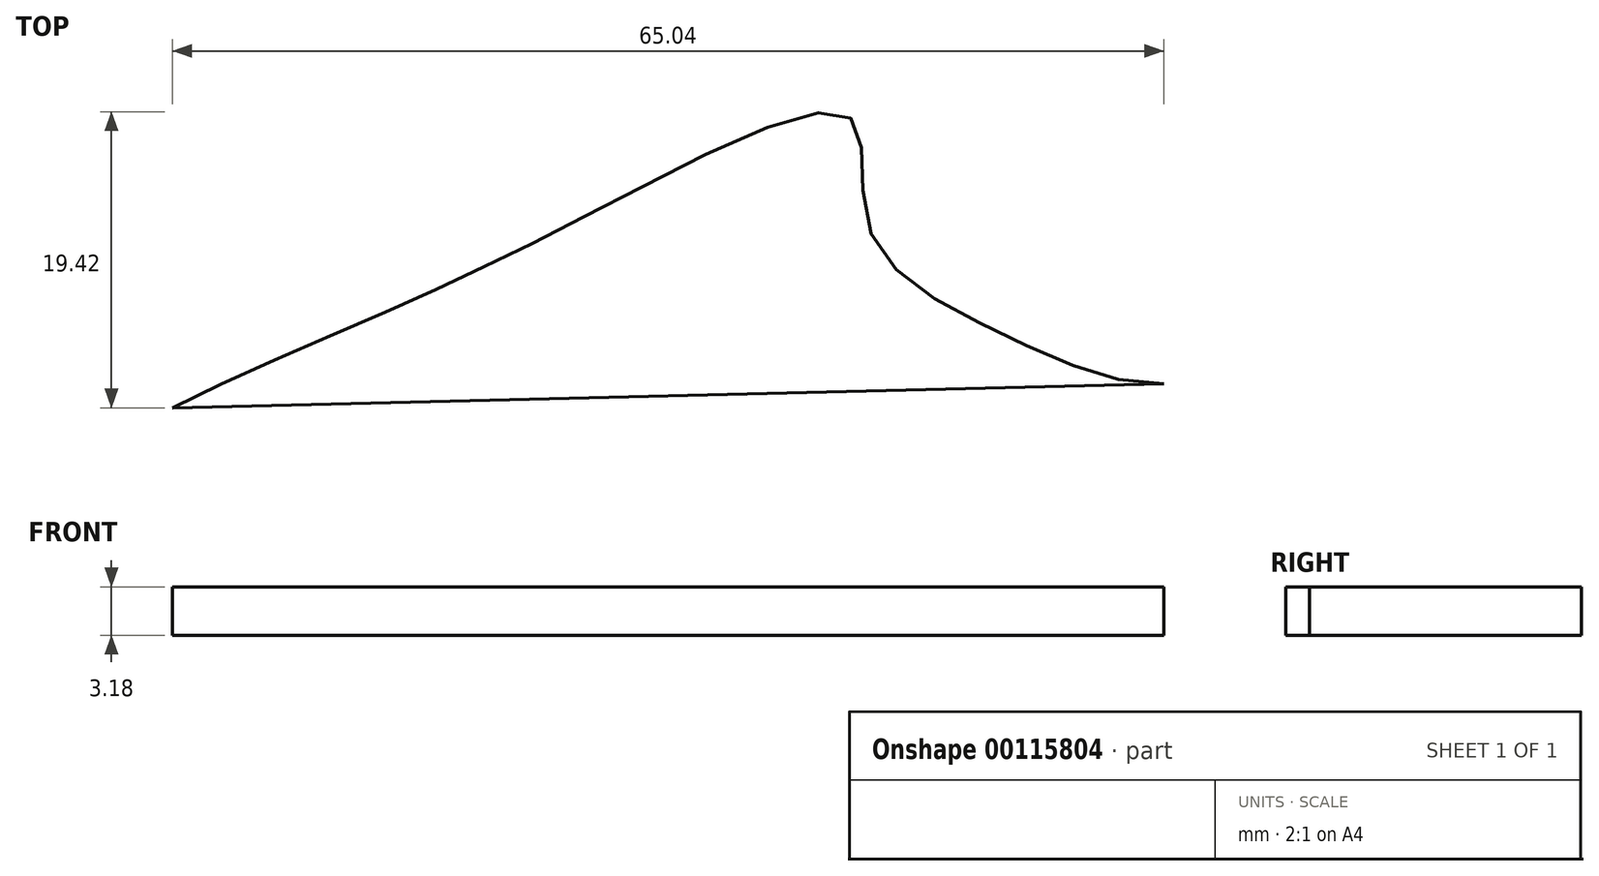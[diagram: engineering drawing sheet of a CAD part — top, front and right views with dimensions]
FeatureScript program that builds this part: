
annotation { "Feature Type Name" : "Feature", "Feature Type Description" : "" }
export const myFeature = defineFeature(function(context is Context, id is Id, definition is map)
    precondition{}
    {
        {
            var Q0;
            Q0=qCreatedBy(makeId("Top.planeOp"),FACE);
            var sketch = newSketch(context, id + "F0", { "sketchPlane" : qUnion([Q0])});
            skFitSpline(sketch, "E0", {"points": [v(-38.84, 12.13) * mm, v(-23.52, 19.01) * mm, v(-9.45, 25.9) * mm, v(5.56, 31.2) * mm, v(6.81, 24.02) * mm, v(15.26, 17.14) * mm, v(26.2, 13.7) * mm], "startDerivative": vector(67.54, 34.24) * mm, "endDerivative": vector(68.55, 1.34) * mm});
            skLineSegment(sketch, "E1", {"start": v(-38.84, 12.13) * mm, "end": v(26.2, 13.7) * mm});
            skSolve(sketch);
        }
        {
            var Q0;
            Q0=makeQuery(id+"F0.imprint","IMPRINT",FACE,{"disambiguationData":[TD([[makeQuery(id+"F0.imprint","IMPRINT",EDGE,{"derivedFrom":sQuery(id+"F0.wireOp",EDGE,"E0")}),-1.0]])]});
            extrude(context, id + "F1", {"entities" : qUnion([Q0]), "depth" : 3.17 * mm});
        }
    });
